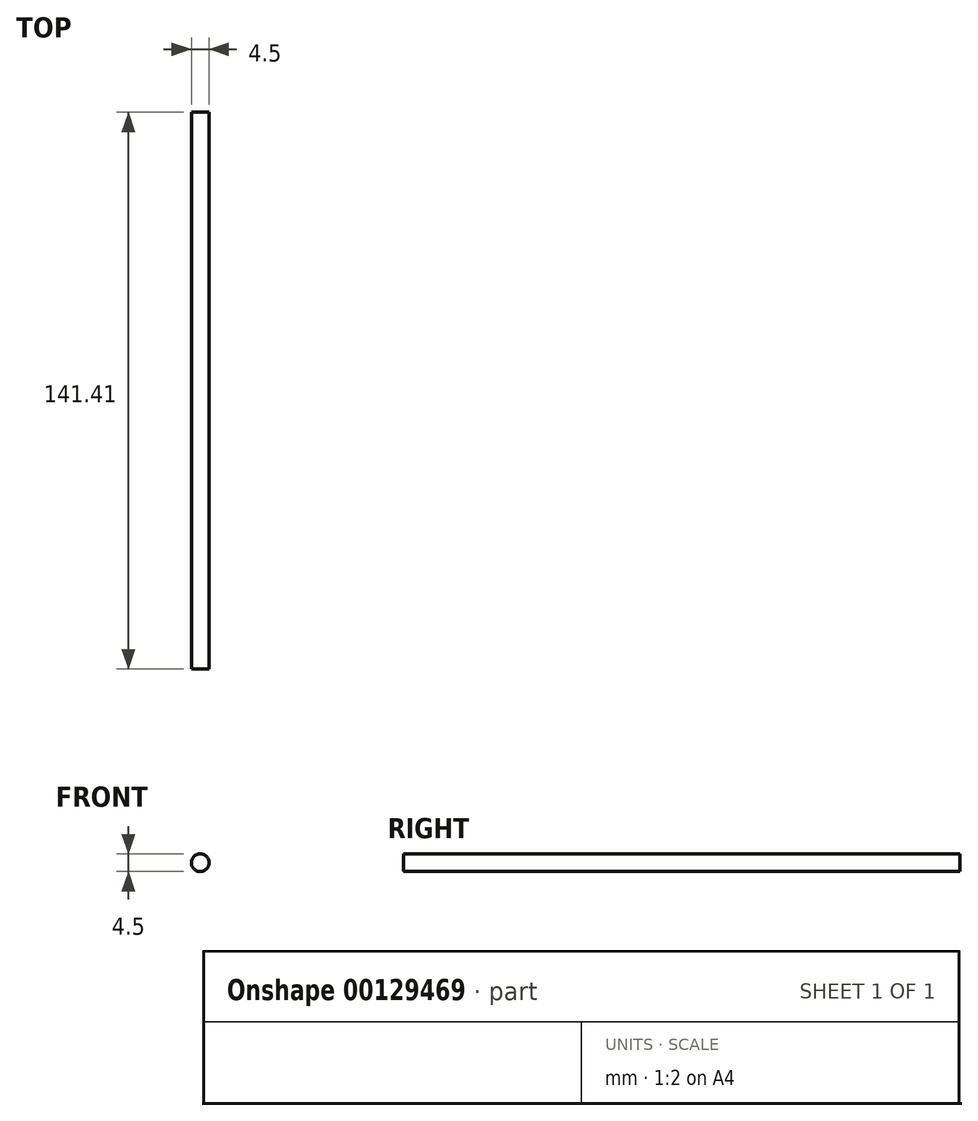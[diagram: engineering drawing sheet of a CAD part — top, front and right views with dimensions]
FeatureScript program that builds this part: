
annotation { "Feature Type Name" : "Feature", "Feature Type Description" : "" }
export const myFeature = defineFeature(function(context is Context, id is Id, definition is map)
    precondition{}
    {
        {
            var Q0;
            Q0=qCreatedBy(makeId("Front.planeOp"),FACE);
            var sketch = newSketch(context, id + "F0", { "sketchPlane" : qUnion([Q0])});
            skCircle(sketch, "E0", {"center": v(0, 0) * mm, "radius": 2.25 * mm});
            skSolve(sketch);
        }
        {
            var Q0;
            Q0=qSketchRegion(id+"F0",true);
            extrude(context, id + "F1", {"entities" : qUnion([Q0]), "depth" : 141.4 * mm});
        }
    });
